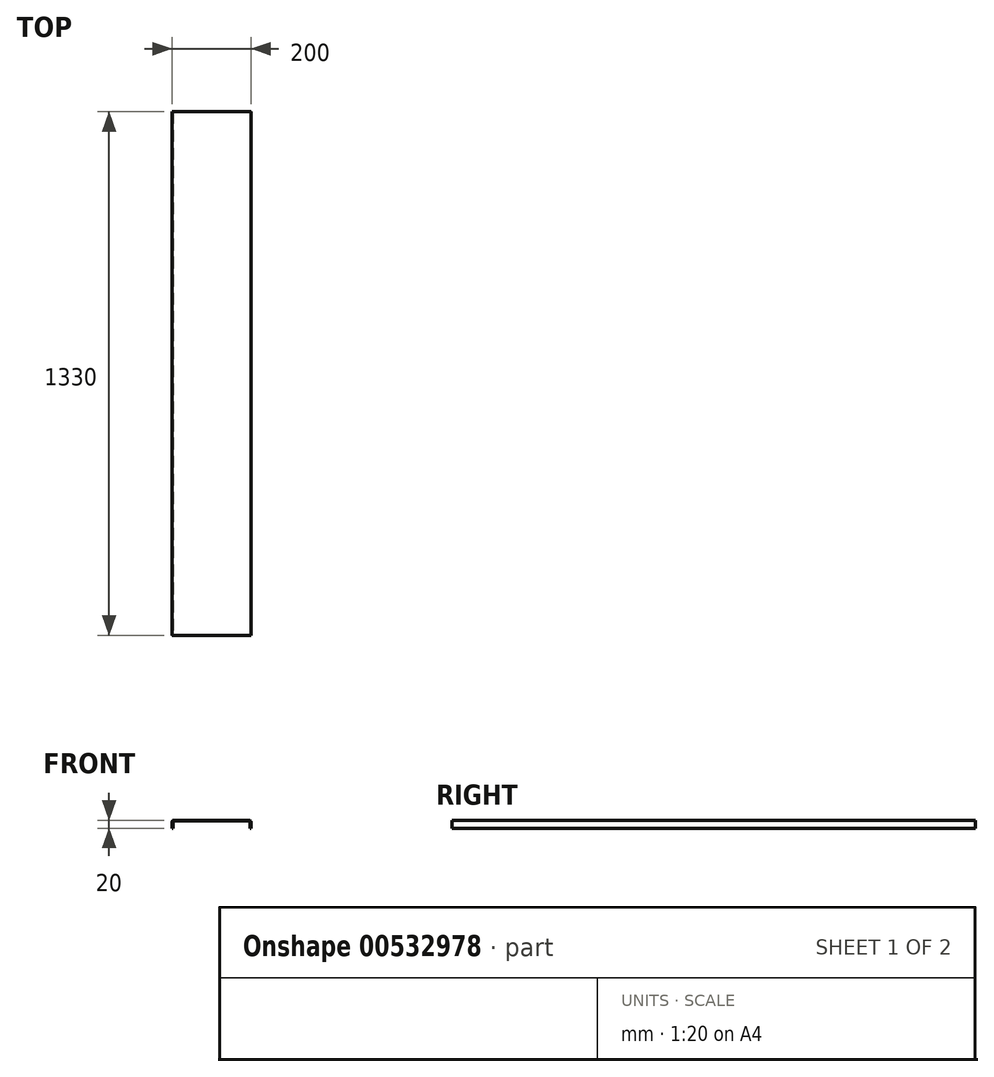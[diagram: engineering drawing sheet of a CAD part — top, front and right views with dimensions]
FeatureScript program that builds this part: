
annotation { "Feature Type Name" : "Feature", "Feature Type Description" : "" }
export const myFeature = defineFeature(function(context is Context, id is Id, definition is map)
    precondition{}
    {
        {
            var Q0;
            Q0=qCreatedBy(makeId("Front.planeOp"),FACE);
            var sketch = newSketch(context, id + "F0", { "sketchPlane" : qUnion([Q0])});
            skLineSegment(sketch, "E0", {"start": v(-69.76, 0) * mm, "end": v(-69.76, 16) * mm});
            skLineSegment(sketch, "E1", {"start": v(-65.76, 20) * mm, "end": v(126.24, 20) * mm});
            skLineSegment(sketch, "E2", {"start": v(130.24, 16) * mm, "end": v(130.24, 0) * mm});
            skLineSegment(sketch, "E3.0", {"start": v(-67.76, 0) * mm, "end": v(-67.76, 16) * mm});
            skLineSegment(sketch, "E4.0", {"start": v(-65.76, 18) * mm, "end": v(126.24, 18) * mm});
            skLineSegment(sketch, "E5.0", {"start": v(128.24, 16) * mm, "end": v(128.24, 0) * mm});
            skLineSegment(sketch, "E6", {"start": v(128.24, 0) * mm, "end": v(130.24, 0) * mm});
            skLineSegment(sketch, "E7", {"start": v(-69.76, 0) * mm, "end": v(-67.76, 0) * mm});
            skPoint(sketch, "E8.visualSharp", {"position": v(128.24, 18) * mm});
            skArc(sketch, "E8.filletArc", {"start": v(128.24, 16) * mm, "mid": v(127.66, 17.41) * mm, "end": v(126.24, 18) * mm});
            skPoint(sketch, "E9.visualSharp", {"position": v(-67.76, 18) * mm});
            skArc(sketch, "E9.filletArc", {"start": v(-65.76, 18) * mm, "mid": v(-67.17, 17.41) * mm, "end": v(-67.76, 16) * mm});
            skPoint(sketch, "E10.visualSharp", {"position": v(-69.76, 20) * mm});
            skArc(sketch, "E10.filletArc", {"start": v(-65.76, 20) * mm, "mid": v(-68.59, 18.83) * mm, "end": v(-69.76, 16) * mm});
            skPoint(sketch, "E11.visualSharp", {"position": v(130.24, 20) * mm});
            skArc(sketch, "E11.filletArc", {"start": v(130.24, 16) * mm, "mid": v(129.07, 18.83) * mm, "end": v(126.24, 20) * mm});
            skSolve(sketch);
        }
        {
            var Q0;
            Q0 = qSketchRegion(id + "F0", true);
            extrude(context, id + "F1", {"entities" : qUnion([Q0]), "oppositeDirection" : true, "depth" : 1330 * mm, "offsetDistance" : 25 * mm});
        }
    });
